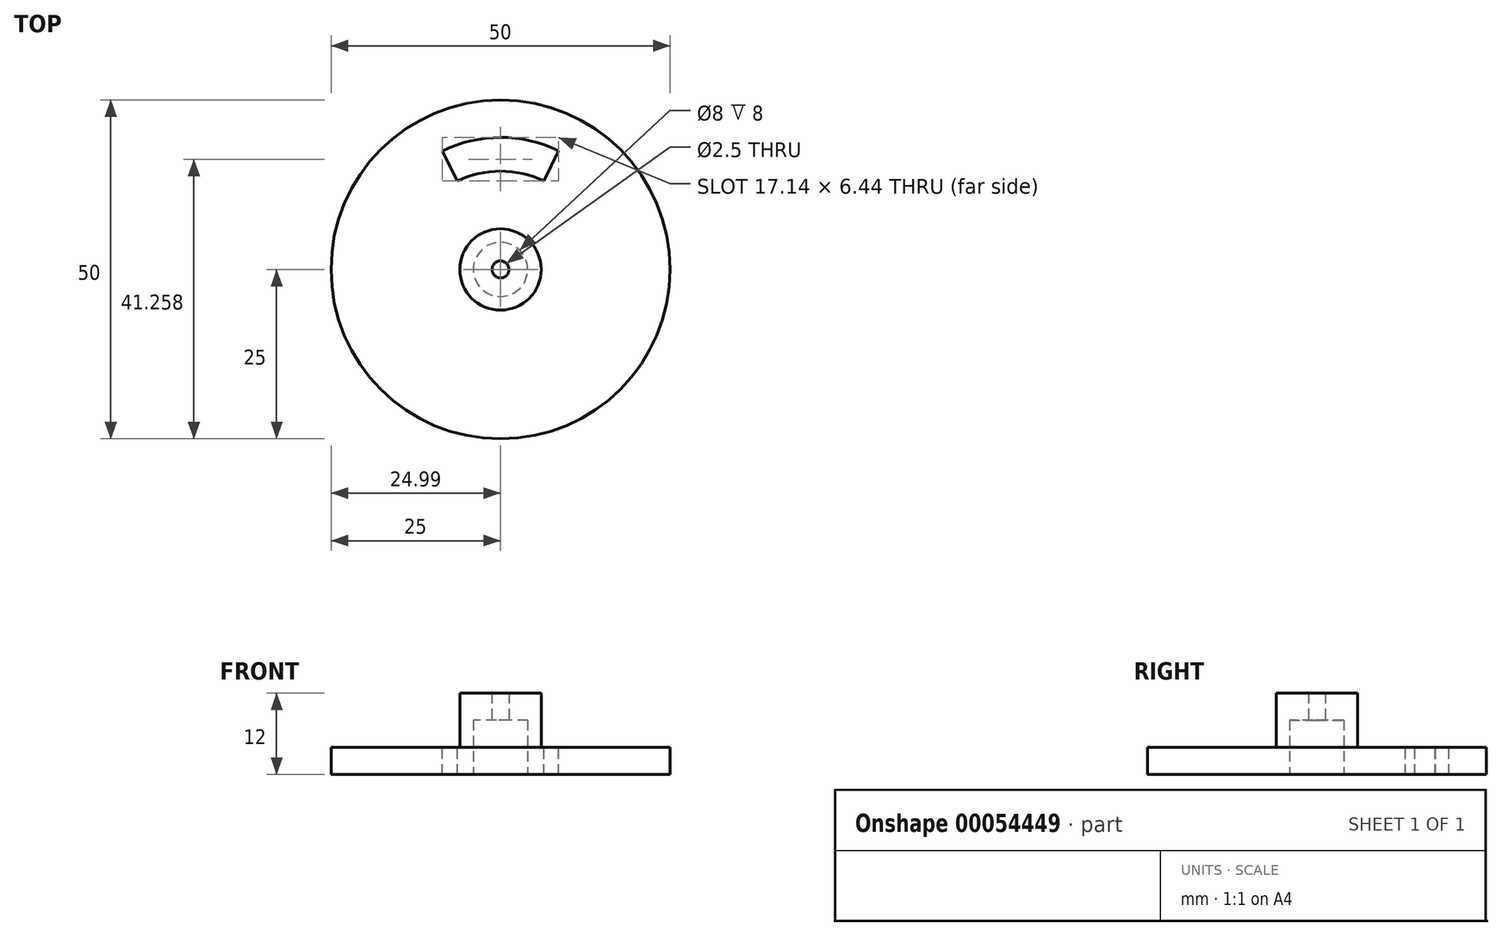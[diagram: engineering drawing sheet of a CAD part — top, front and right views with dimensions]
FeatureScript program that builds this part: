
annotation { "Feature Type Name" : "Feature", "Feature Type Description" : "" }
export const myFeature = defineFeature(function(context is Context, id is Id, definition is map)
    precondition{}
    {
        {
            var Q0;
            Q0=qCreatedBy(makeId("Top.planeOp"),FACE);
            var sketch = newSketch(context, id + "F0", { "sketchPlane" : qUnion([Q0])});
            skCircle(sketch, "E0", {"center": v(0, 0) * mm, "radius": 25 * mm});
            skCircle(sketch, "E1", {"center": v(0, 0) * mm, "radius": 4 * mm});
            skCircle(sketch, "E2", {"center": v(0, 0) * mm, "radius": 6 * mm});
            skSolve(sketch);
        }
        {
            var Q0;
            Q0=makeQuery(id+"F0.imprint","IMPRINT",FACE,{"disambiguationData":[TD([[makeQuery(id+"F0.imprint","IMPRINT",EDGE,{"derivedFrom":sQuery(id+"F0.wireOp",EDGE,"E0")}),1.0]])]});
            extrude(context, id + "F1", {"entities" : qUnion([Q0]), "depth" : 4 * mm});
        }
        {
            var Q0;
            Q0=makeQuery(id+"F0.imprint","IMPRINT",FACE,{"disambiguationData":[TD([[makeQuery(id+"F0.imprint","IMPRINT",EDGE,{"derivedFrom":sQuery(id+"F0.wireOp",EDGE,"E1")}),-1.0]])]});
            extrude(context, id + "F2", {"entities" : qUnion([Q0]), "operationType" : NewBodyOperationType.ADD, "depth" : 8 * mm});
        }
        {
            var Q0;
            Q0=makeQuery(id+"F1.opExtrude","CAP_FACE",FACE,{"disambiguationData":[OSD([sQuery(id+"F0.wireOp",EDGE,"E0"),sQuery(id+"F0.wireOp",EDGE,"E2")])],"isStart":false});
            var sketch = newSketch(context, id + "F3", { "sketchPlane" : qUnion([Q0])});
            skCircle(sketch, "E3", {"center": v(0, 0) * mm, "radius": 14.5 * mm, "construction": true});
            skCircle(sketch, "E4", {"center": v(0, 0) * mm, "radius": 19.5 * mm, "construction": true});
            skLineSegment(sketch, "E5", {"start": v(0, 0) * mm, "end": v(0, 17) * mm, "construction": true});
            skLineSegment(sketch, "E6", {"start": v(0, 0) * mm, "end": v(8.55, 17.53) * mm, "construction": true});
            skLineSegment(sketch, "E7", {"start": v(0, 0) * mm, "end": v(-8.55, 17.53) * mm, "construction": true});
            skSolve(sketch);
        }
        {
            var Q0;
            Q0=makeQuery(id+"F3.imprint","IMPRINT",FACE,{"disambiguationData":[TD([[makeQuery(id+"F3.imprint","IMPRINT",EDGE,{"derivedFrom":makeQuery(id+"F1.opExtrude","CAP_EDGE",EDGE,{"disambiguationData":[OSD([sQuery(id+"F0.wireOp",EDGE,"E0")])],"isStart":false})}),1.0]])]});
            var sketch = newSketch(context, id + "F4", { "sketchPlane" : qUnion([Q0])});
            skLineSegment(sketch, "E8", {"start": v(-8.58, 17.48) * mm, "end": v(-6.36, 13.04) * mm});
            skLineSegment(sketch, "E9", {"start": v(8.56, 17.52) * mm, "end": v(6.39, 13.04) * mm});
            skArc(sketch, "E10", {"start": v(6.39, 13.04) * mm, "mid": v(0.01, 14.5) * mm, "end": v(-6.36, 13.04) * mm});
            skArc(sketch, "E11", {"start": v(8.56, 17.52) * mm, "mid": v(-0.02, 19.48) * mm, "end": v(-8.58, 17.48) * mm});
            skSolve(sketch);
        }
        {
            var Q0;
            Q0 = qSketchRegion(id + "F4", true);
            extrude(context, id + "F5", {"entities" : qUnion([Q0]), "operationType" : NewBodyOperationType.REMOVE, "oppositeDirection" : true, "depth" : 25 * mm});
        }
        {
            var Q0;
            Q0=makeQuery(id+"F2.opExtrude","CAP_FACE",FACE,{"disambiguationData":[OSD([sQuery(id+"F0.wireOp",EDGE,"E1"),sQuery(id+"F0.wireOp",EDGE,"E2")])],"isStart":false});
            var sketch = newSketch(context, id + "F6", { "sketchPlane" : qUnion([Q0])});
            skCircle(sketch, "E12", {"center": v(0, 0) * mm, "radius": 6 * mm});
            skCircle(sketch, "E13", {"center": v(0, 0) * mm, "radius": 1.25 * mm});
            skSolve(sketch);
        }
        {
            var Q0;
            Q0 = qSketchRegion(id + "F6", true);
            extrude(context, id + "F7", {"entities" : qUnion([Q0]), "operationType" : NewBodyOperationType.ADD, "depth" : 4 * mm});
        }
    });
